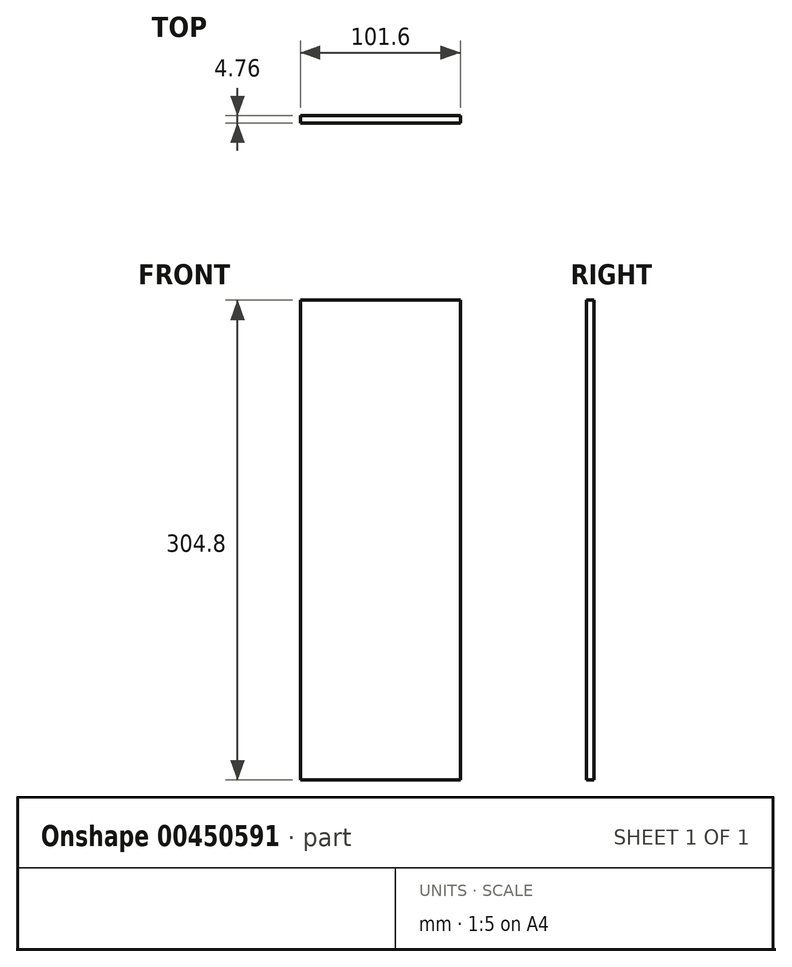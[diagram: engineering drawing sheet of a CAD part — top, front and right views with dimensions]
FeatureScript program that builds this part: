
annotation { "Feature Type Name" : "Feature", "Feature Type Description" : "" }
export const myFeature = defineFeature(function(context is Context, id is Id, definition is map)
    precondition{}
    {
        {
            var Q0;
            Q0=qCreatedBy(makeId("Front.planeOp"),FACE);
            var sketch = newSketch(context, id + "F0", { "sketchPlane" : qUnion([Q0])});
            skLineSegment(sketch, "E0.bottom", {"start": v(-101.43, 87.09) * mm, "end": v(-203.03, 87.09) * mm});
            skLineSegment(sketch, "E0.top", {"start": v(-101.43, -217.71) * mm, "end": v(-203.03, -217.71) * mm});
            skLineSegment(sketch, "E0.left", {"start": v(-101.43, 87.09) * mm, "end": v(-101.43, -217.71) * mm});
            skLineSegment(sketch, "E0.right", {"start": v(-203.03, 87.09) * mm, "end": v(-203.03, -217.71) * mm});
            skSolve(sketch);
        }
        {
            var Q0;
            Q0=makeQuery(id+"F0.imprint","IMPRINT",FACE,{"disambiguationData":[TD([[makeQuery(id+"F0.imprint","IMPRINT",EDGE,{"derivedFrom":sQuery(id+"F0.wireOp",EDGE,"E0.bottom")}),1.0]])]});
            extrude(context, id + "F1", {"entities" : qUnion([Q0]), "depth" : 4.76 * mm});
        }
    });
